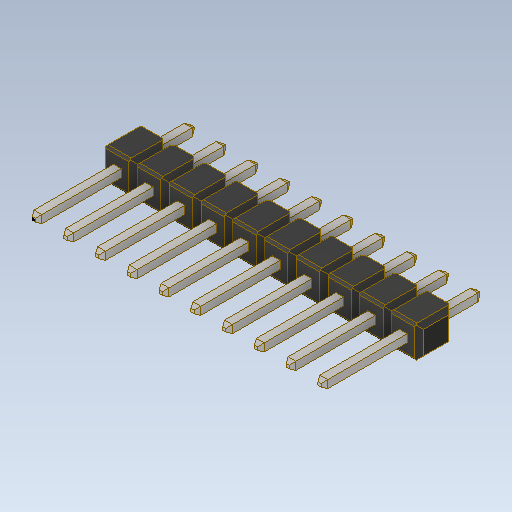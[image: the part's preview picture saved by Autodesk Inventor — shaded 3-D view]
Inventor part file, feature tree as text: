
AUTODESK INVENTOR PART (.ipt)
format: ipt  version: 2020.3 (Build 243373000, 373)  size: 470,016 bytes
history: native  units: mm
features: other x20, shell x10, sketch x1
ambient origin geometry x8: Origin, YZ Plane, XZ Plane, XY Plane, X Axis, Y Axis, Z Axis, Center Point
bodies: Solid1 (feature_tree), Solid2 (feature_tree), Solid3 (feature_tree), Solid4 (feature_tree), Solid5 (feature_tree), Solid6 (feature_tree), Solid7 (feature_tree), Solid8 (feature_tree), Solid9 (feature_tree), Solid10 (feature_tree)
feature tree (31):
  sketch  "Sketch1"
  other  "brep_1"
  other  "brep_2"
  other  "brep_3"
  other  "brep_4"
  other  "brep_5"
  other  "brep_6"
  other  "brep_7"
  other  "brep_8"
  other  "brep_9"
  other  "brep_10"
  shell  "shell_1"  [1 undecoded]
  shell  "shell_2"  [1 undecoded]
  shell  "shell_3"  [1 undecoded]
  shell  "shell_4"  [1 undecoded]
  shell  "shell_5"  [1 undecoded]
  shell  "shell_6"  [1 undecoded]
  shell  "shell_7"  [1 undecoded]
  shell  "shell_8"  [1 undecoded]
  shell  "shell_9"  [1 undecoded]
  shell  "shell_10"  [1 undecoded]
  other  "Srf1"
  other  "Srf2"
  other  "Srf3"
  other  "Srf4"
  other  "Srf5"
  other  "Srf6"
  other  "Srf7"
  other  "Srf8"
  other  "Srf9"
  other  "Srf10"
note: 10 required parameter values undecoded (feature->parameter linkage not recoverable at this tier; creation-order binding heuristic only, values carry confidence <= 0.55)
